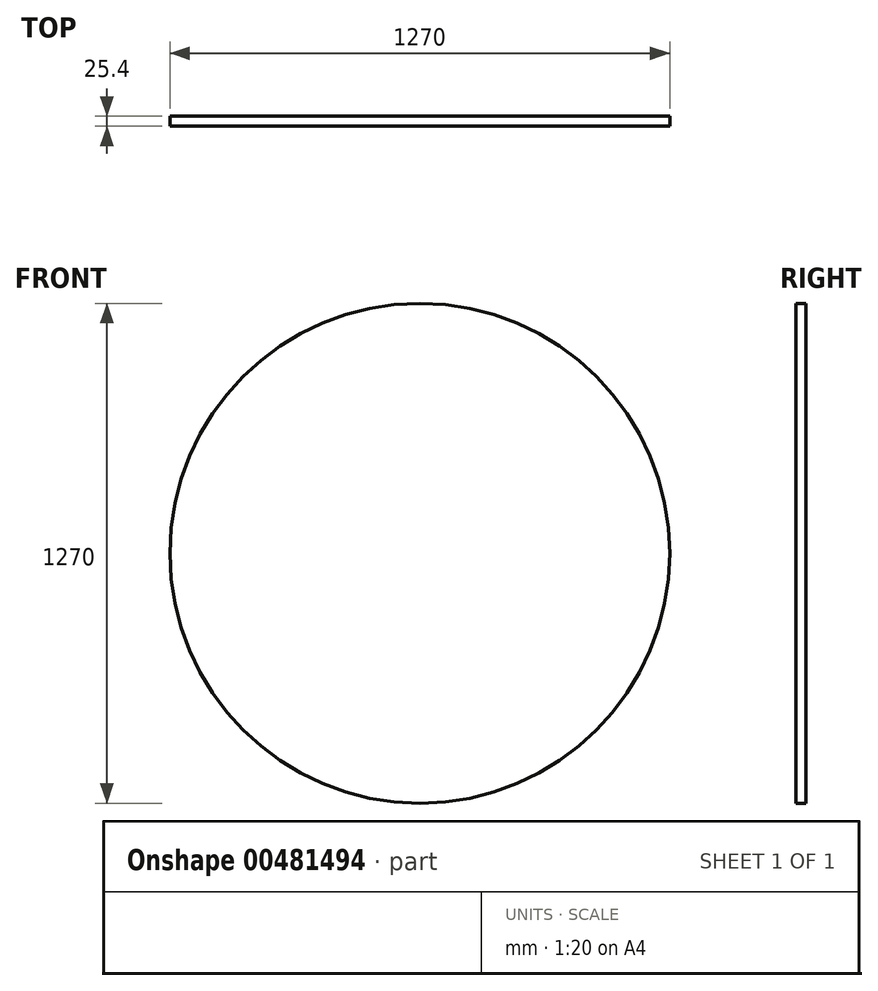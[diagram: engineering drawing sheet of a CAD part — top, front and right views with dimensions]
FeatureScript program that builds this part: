
annotation { "Feature Type Name" : "Feature", "Feature Type Description" : "" }
export const myFeature = defineFeature(function(context is Context, id is Id, definition is map)
    precondition{}
    {
        {
            var Q0;
            Q0=qCreatedBy(makeId("Front.planeOp"),FACE);
            var sketch = newSketch(context, id + "F0", { "sketchPlane" : qUnion([Q0])});
            skCircle(sketch, "E0", {"center": v(0, 0) * mm, "radius": 635 * mm});
            skSolve(sketch);
        }
        {
            var Q0;
            Q0 = qSketchRegion(id + "F0", true);
            extrude(context, id + "F1", {"entities" : qUnion([Q0]), "depth" : 25.4 * mm});
        }
    });
